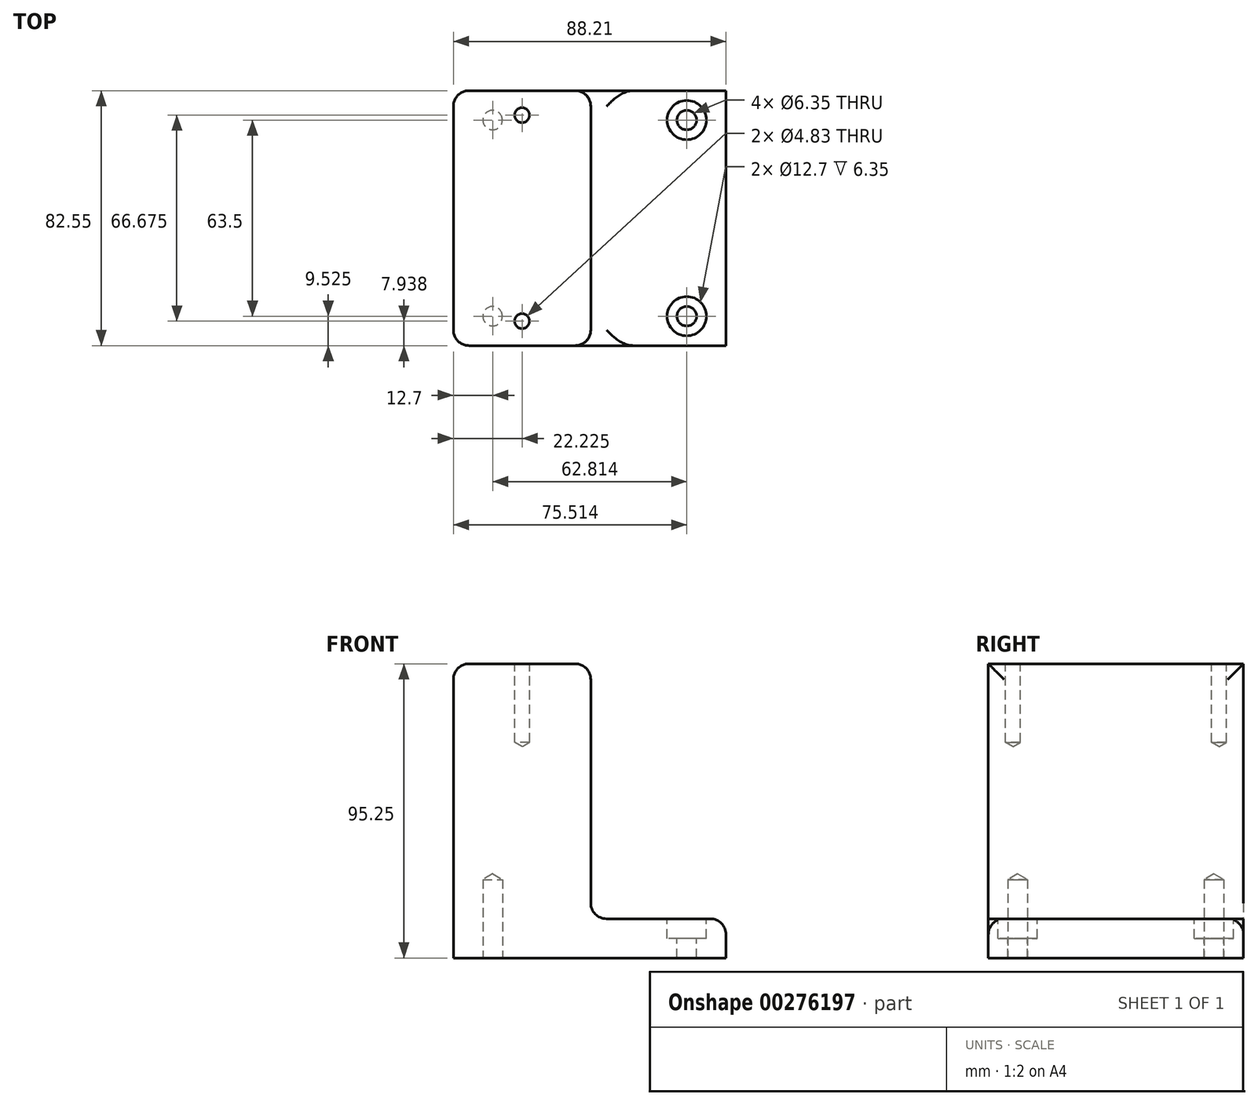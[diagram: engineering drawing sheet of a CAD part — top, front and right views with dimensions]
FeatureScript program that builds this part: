
annotation { "Feature Type Name" : "Feature", "Feature Type Description" : "" }
export const myFeature = defineFeature(function(context is Context, id is Id, definition is map)
    precondition{}
    {
        {
            var Q0;
            Q0=qCreatedBy(makeId("Front.planeOp"),FACE);
            var sketch = newSketch(context, id + "F0", { "sketchPlane" : qUnion([Q0])});
            skLineSegment(sketch, "E0", {"start": v(0, 0) * mm, "end": v(0, 95.25) * mm});
            skLineSegment(sketch, "E1", {"start": v(0, 95.25) * mm, "end": v(44.45, 95.25) * mm});
            skLineSegment(sketch, "E2", {"start": v(44.45, 95.25) * mm, "end": v(44.45, 12.7) * mm});
            skLineSegment(sketch, "E3", {"start": v(44.45, 12.7) * mm, "end": v(88.21, 12.7) * mm});
            skLineSegment(sketch, "E4", {"start": v(88.21, 12.7) * mm, "end": v(88.21, 0) * mm});
            skLineSegment(sketch, "E5", {"start": v(88.21, 0) * mm, "end": v(0, 0) * mm});
            skSolve(sketch);
        }
        {
            var Q0;
            Q0=makeQuery(id+"F0.imprint","IMPRINT",FACE,{"disambiguationData":[TD([[makeQuery(id+"F0.imprint","IMPRINT",EDGE,{"derivedFrom":sQuery(id+"F0.wireOp",EDGE,"E0")}),-1.0]])]});
            extrude(context, id + "F1", {"entities" : qUnion([Q0]), "depth" : 82.55 * mm});
        }
        {
            var Q0;
            Q0=makeQuery(id+"F1.opExtrude","SWEPT_EDGE",EDGE,{"disambiguationData":[OSD([sQuery(id+"F0.wireOp",EDGE,"E2"),sQuery(id+"F0.wireOp",EDGE,"E3")])]});
            var Q1;
            Q1=makeQuery(id+"F1.opExtrude","SWEPT_EDGE",EDGE,{"disambiguationData":[OSD([sQuery(id+"F0.wireOp",EDGE,"E1"),sQuery(id+"F0.wireOp",EDGE,"E2")])]});
            var Q2;
            Q2=makeQuery(id+"F1.opExtrude","SWEPT_EDGE",EDGE,{"disambiguationData":[OSD([sQuery(id+"F0.wireOp",EDGE,"E0"),sQuery(id+"F0.wireOp",EDGE,"E1")])]});
            var Q3;
            Q3=makeQuery(id+"F1.opExtrude","CAP_EDGE",EDGE,{"disambiguationData":[OSD([sQuery(id+"F0.wireOp",EDGE,"E2")])],"isStart":false});
            var Q4;
            Q4=makeQuery(id+"F1.opExtrude","CAP_EDGE",EDGE,{"disambiguationData":[OSD([sQuery(id+"F0.wireOp",EDGE,"E2")])],"isStart":true});
            var Q5;
            Q5=makeQuery(id+"F1.opExtrude","CAP_EDGE",EDGE,{"disambiguationData":[OSD([sQuery(id+"F0.wireOp",EDGE,"E0")])],"isStart":false});
            var Q6;
            Q6=makeQuery(id+"F1.opExtrude","CAP_EDGE",EDGE,{"disambiguationData":[OSD([sQuery(id+"F0.wireOp",EDGE,"E0")])],"isStart":true});
            var Q7;
            Q7=makeQuery(id+"F1.opExtrude","SWEPT_EDGE",EDGE,{"disambiguationData":[OSD([sQuery(id+"F0.wireOp",EDGE,"E3"),sQuery(id+"F0.wireOp",EDGE,"E4")])]});
            fillet(context, id + "F2", {"entities" : qUnion([Q0, Q1, Q2, Q3, Q4, Q5, Q6, Q7]), "radius" : 5.08 * mm, "tangentPropagation" : true, "allowEdgeOverflow" : false});
        }
        {
            var Q0;
            Q0=makeQuery(id+"F1.opExtrude","SWEPT_FACE",FACE,{"disambiguationData":[OSD([sQuery(id+"F0.wireOp",EDGE,"E1")])]});
            var sketch = newSketch(context, id + "F3", { "sketchPlane" : qUnion([Q0])});
            skLineSegment(sketch, "E6", {"start": v(5.08, -41.28) * mm, "end": v(39.37, -41.28) * mm, "construction": true});
            skPoint(sketch, "E7", {"position": v(22.23, -7.94) * mm});
            skPoint(sketch, "E7.positionSnap0", {"position": v(22.23, -41.28) * mm});
            skPoint(sketch, "E8.MirrorP", {"position": v(22.23, -74.61) * mm});
            skSolve(sketch);
        }
        {
            var Q0;
            Q0=sQuery(id+"F3.wireOp",VERTEX,"E7");
            var Q1;
            Q1=sQuery(id+"F3.wireOp",VERTEX,"E8.MirrorP");
            var Q2;
            Q2=makeQuery(id+"F1.opExtrude","SWEPT_BODY",BODY,{"disambiguationData":[OSD([sQuery(id+"F0.wireOp",EDGE,"E0"),sQuery(id+"F0.wireOp",EDGE,"E1"),sQuery(id+"F0.wireOp",EDGE,"E2"),sQuery(id+"F0.wireOp",EDGE,"E3"),sQuery(id+"F0.wireOp",EDGE,"E4"),sQuery(id+"F0.wireOp",EDGE,"E5")])]});
            hole(context, id + "F4", {"style" : HoleStyle.SIMPLE, "endStyle" : HoleEndStyle.BLIND, "holeDiameter" : 4.83 * mm, "holeDepth" : 25.4 * mm, "tappedDepth" : 12.7 * mm, "tapClearance" : 3, "locations" : qUnion([Q0, Q1]), "scope" : qUnion([Q2])});
        }
        {
            var Q0;
            Q0=makeQuery(id+"F1.opExtrude","SWEPT_FACE",FACE,{"disambiguationData":[OSD([sQuery(id+"F0.wireOp",EDGE,"E5")])]});
            var sketch = newSketch(context, id + "F5", { "sketchPlane" : qUnion([Q0])});
            skLineSegment(sketch, "E9", {"start": v(0, 41.28) * mm, "end": v(88.21, 41.28) * mm, "construction": true});
            skPoint(sketch, "E10", {"position": v(12.7, 73.03) * mm});
            skPoint(sketch, "E11.MirrorP", {"position": v(12.7, 9.53) * mm});
            skSolve(sketch);
        }
        {
            var Q0;
            Q0=sQuery(id+"F5.wireOp",VERTEX,"E10");
            var Q1;
            Q1=sQuery(id+"F5.wireOp",VERTEX,"E11.MirrorP");
            var Q2;
            Q2=makeQuery(id+"F1.opExtrude","SWEPT_BODY",BODY,{"disambiguationData":[OSD([sQuery(id+"F0.wireOp",EDGE,"E0"),sQuery(id+"F0.wireOp",EDGE,"E1"),sQuery(id+"F0.wireOp",EDGE,"E2"),sQuery(id+"F0.wireOp",EDGE,"E3"),sQuery(id+"F0.wireOp",EDGE,"E4"),sQuery(id+"F0.wireOp",EDGE,"E5")])]});
            hole(context, id + "F6", {"style" : HoleStyle.SIMPLE, "endStyle" : HoleEndStyle.BLIND, "holeDiameter" : 6.35 * mm, "holeDepth" : 25.4 * mm, "tappedDepth" : 12.7 * mm, "tapClearance" : 3, "locations" : qUnion([Q0, Q1]), "scope" : qUnion([Q2])});
        }
        {
            var Q0;
            Q0=makeQuery(id+"F1.opExtrude","SWEPT_FACE",FACE,{"disambiguationData":[OSD([sQuery(id+"F0.wireOp",EDGE,"E3")])]});
            var sketch = newSketch(context, id + "F7", { "sketchPlane" : qUnion([Q0])});
            skLineSegment(sketch, "E12", {"start": v(49.53, -41.28) * mm, "end": v(83.13, -41.28) * mm, "construction": true});
            skPoint(sketch, "E13", {"position": v(75.51, -9.53) * mm});
            skPoint(sketch, "E14.MirrorP", {"position": v(75.51, -73.03) * mm});
            skSolve(sketch);
        }
        {
            var Q0;
            Q0=sQuery(id+"F7.wireOp",VERTEX,"E13");
            var Q1;
            Q1=sQuery(id+"F7.wireOp",VERTEX,"E14.MirrorP");
            var Q2;
            Q2=makeQuery(id+"F1.opExtrude","SWEPT_BODY",BODY,{"disambiguationData":[OSD([sQuery(id+"F0.wireOp",EDGE,"E0"),sQuery(id+"F0.wireOp",EDGE,"E1"),sQuery(id+"F0.wireOp",EDGE,"E2"),sQuery(id+"F0.wireOp",EDGE,"E3"),sQuery(id+"F0.wireOp",EDGE,"E4"),sQuery(id+"F0.wireOp",EDGE,"E5")])]});
            hole(context, id + "F8", {"style" : HoleStyle.C_BORE, "endStyle" : HoleEndStyle.BLIND, "holeDiameter" : 6.35 * mm, "cBoreDiameter" : 12.7 * mm, "cBoreDepth" : 6.35 * mm, "holeDepth" : 25.4 * mm, "tappedDepth" : 12.7 * mm, "tapClearance" : 3, "locations" : qUnion([Q0, Q1]), "scope" : qUnion([Q2])});
        }
    });
